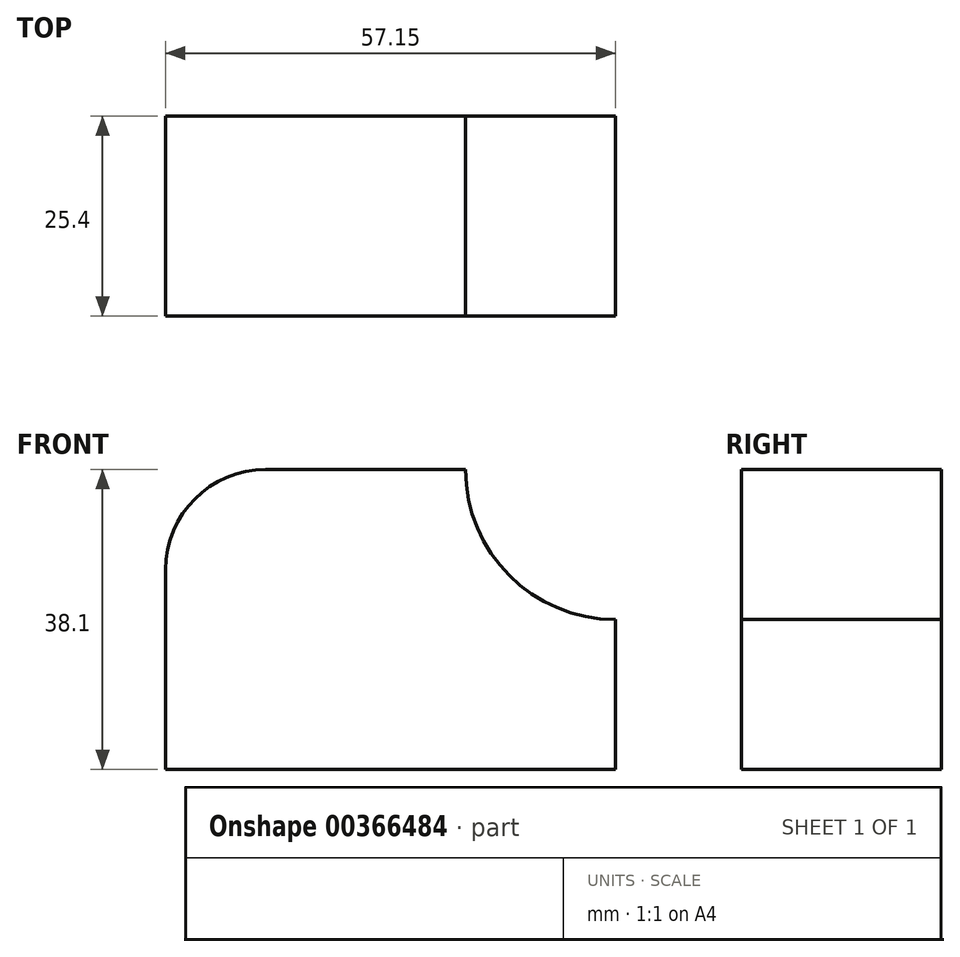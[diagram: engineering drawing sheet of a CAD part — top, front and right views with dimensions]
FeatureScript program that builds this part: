
annotation { "Feature Type Name" : "Feature", "Feature Type Description" : "" }
export const myFeature = defineFeature(function(context is Context, id is Id, definition is map)
    precondition{}
    {
        {
            var Q0;
            Q0=qCreatedBy(makeId("Front.planeOp"),FACE);
            var sketch = newSketch(context, id + "F0", { "sketchPlane" : qUnion([Q0])});
            skLineSegment(sketch, "E0", {"start": v(0, 0) * mm, "end": v(0, 38.1) * mm});
            skLineSegment(sketch, "E1", {"start": v(0, 38.1) * mm, "end": v(57.15, 38.1) * mm});
            skLineSegment(sketch, "E2", {"start": v(57.15, 38.1) * mm, "end": v(57.15, 0) * mm});
            skLineSegment(sketch, "E3", {"start": v(57.15, 0) * mm, "end": v(0, 0) * mm});
            skSolve(sketch);
        }
        {
            var Q0;
            Q0 = qSketchRegion(id + "F0", true);
            extrude(context, id + "F1", {"entities" : qUnion([Q0]), "oppositeDirection" : true, "depth" : 25.4 * mm});
        }
        {
            var Q0;
            Q0=makeQuery(id+"F1.opExtrude","CAP_FACE",FACE,{"disambiguationData":[OSD([sQuery(id+"F0.wireOp",EDGE,"E0"),sQuery(id+"F0.wireOp",EDGE,"E1"),sQuery(id+"F0.wireOp",EDGE,"E2"),sQuery(id+"F0.wireOp",EDGE,"E3")])],"isStart":true});
            var sketch = newSketch(context, id + "F2", { "sketchPlane" : qUnion([Q0])});
            skArc(sketch, "E4", {"start": v(38.1, 38.1) * mm, "mid": v(43.68, 24.63) * mm, "end": v(57.15, 19.05) * mm});
            skSolve(sketch);
        }
        {
            var Q0;
            Q0 = qSketchRegion(id + "F2", true);
            var Q1;
            {var subQ0=sQuery(id+"F2.wireOp",EDGE,"E4");Q1=makeQuery(id+"F2.imprint","IMPRINT",FACE,{"disambiguationData":[TD([[makeQuery(id+"F2.imprint","IMPRINT",EDGE,{"derivedFrom":subQ0}),1.0]])]});}
            extrude(context, id + "F3", {"entities" : qUnion([Q0, Q1]), "operationType" : NewBodyOperationType.REMOVE, "oppositeDirection" : true, "depth" : 25.4 * mm});
        }
        {
            var Q0;
            Q0=makeQuery(id+"F1.opExtrude","SWEPT_EDGE",EDGE,{"disambiguationData":[OSD([sQuery(id+"F0.wireOp",EDGE,"E0"),sQuery(id+"F0.wireOp",EDGE,"E1")])]});
            fillet(context, id + "F4", {"entities" : qUnion([Q0]), "radius" : 12.7 * mm, "tangentPropagation" : true, "allowEdgeOverflow" : false});
        }
    });
